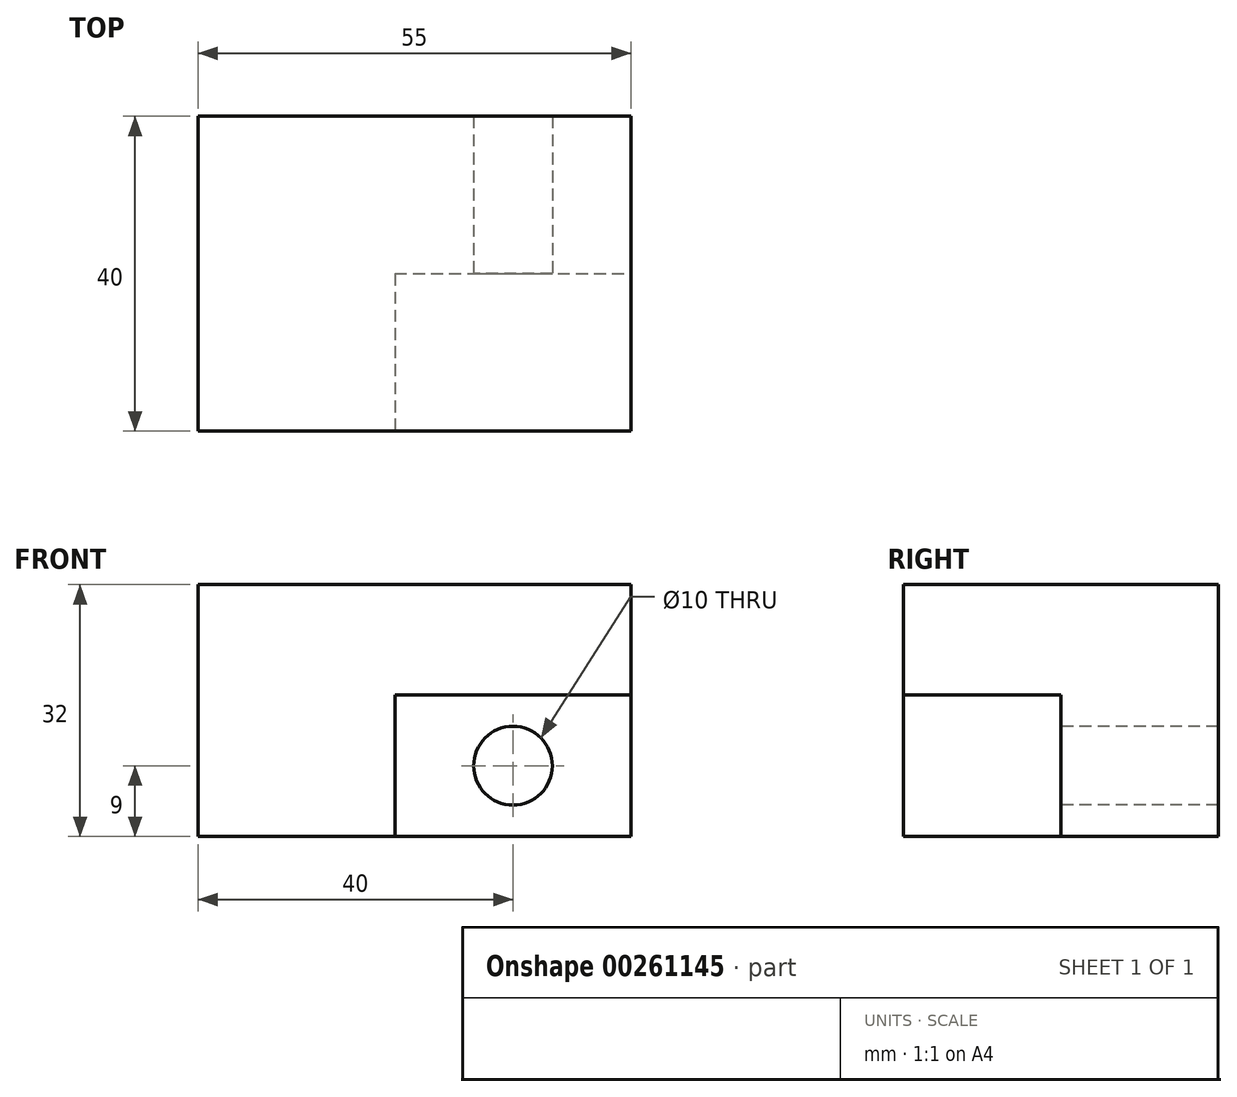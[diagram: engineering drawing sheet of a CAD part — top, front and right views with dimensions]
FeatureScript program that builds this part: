
annotation { "Feature Type Name" : "Feature", "Feature Type Description" : "" }
export const myFeature = defineFeature(function(context is Context, id is Id, definition is map)
    precondition{}
    {
        {
            var Q0;
            Q0=qCreatedBy(makeId("Front.planeOp"),FACE);
            var sketch = newSketch(context, id + "F0", { "sketchPlane" : qUnion([Q0])});
            skLineSegment(sketch, "E0.bottom", {"start": v(0, 0) * mm, "end": v(55, 0) * mm});
            skLineSegment(sketch, "E0.top", {"start": v(0, -32) * mm, "end": v(55, -32) * mm});
            skLineSegment(sketch, "E0.left", {"start": v(0, 0) * mm, "end": v(0, -32) * mm});
            skLineSegment(sketch, "E0.right", {"start": v(55, 0) * mm, "end": v(55, -32) * mm});
            skSolve(sketch);
        }
        {
            var Q0;
            Q0=makeQuery(id+"F0.imprint","IMPRINT",FACE,{"disambiguationData":[TD([[makeQuery(id+"F0.imprint","IMPRINT",EDGE,{"derivedFrom":sQuery(id+"F0.wireOp",EDGE,"E0.bottom")}),-1.0]])]});
            extrude(context, id + "F1", {"entities" : qUnion([Q0]), "depth" : 40 * mm});
        }
        {
            var Q0;
            Q0=makeQuery(id+"F1.opExtrude","CAP_FACE",FACE,{"disambiguationData":[OSD([sQuery(id+"F0.wireOp",EDGE,"E0.bottom"),sQuery(id+"F0.wireOp",EDGE,"E0.top"),sQuery(id+"F0.wireOp",EDGE,"E0.left"),sQuery(id+"F0.wireOp",EDGE,"E0.right")])],"isStart":false});
            var sketch = newSketch(context, id + "F2", { "sketchPlane" : qUnion([Q0])});
            skLineSegment(sketch, "E1.bottom", {"start": v(55, -32) * mm, "end": v(25, -32) * mm});
            skLineSegment(sketch, "E1.top", {"start": v(55, -14) * mm, "end": v(25, -14) * mm});
            skLineSegment(sketch, "E1.left", {"start": v(55, -32) * mm, "end": v(55, -14) * mm});
            skLineSegment(sketch, "E1.right", {"start": v(25, -32) * mm, "end": v(25, -14) * mm});
            skSolve(sketch);
        }
        {
            var Q0;
            Q0=makeQuery(id+"F2.imprint","IMPRINT",FACE,{"disambiguationData":[TD([[makeQuery(id+"F2.imprint","IMPRINT",EDGE,{"derivedFrom":sQuery(id+"F2.wireOp",EDGE,"E1.bottom")}),1.0]])]});
            extrude(context, id + "F3", {"entities" : qUnion([Q0]), "operationType" : NewBodyOperationType.REMOVE, "oppositeDirection" : true, "depth" : 20 * mm});
        }
        {
            var Q0;
            Q0=makeQuery(id+"F3.boolean.opBoolean","COPY",FACE,{"derivedFrom":makeQuery(id+"F3.opExtrude","CAP_FACE",FACE,{"disambiguationData":[OSD([sQuery(id+"F2.wireOp",EDGE,"E1.bottom"),sQuery(id+"F2.wireOp",EDGE,"E1.top"),sQuery(id+"F2.wireOp",EDGE,"E1.left"),sQuery(id+"F2.wireOp",EDGE,"E1.right")])],"isStart":false})});
            var sketch = newSketch(context, id + "F4", { "sketchPlane" : qUnion([Q0])});
            skCircle(sketch, "E2", {"center": v(40, -23) * mm, "radius": 5 * mm});
            skPoint(sketch, "E2.centerSnap0", {"position": v(55, -23) * mm});
            skPoint(sketch, "E2.centerSnap1", {"position": v(40, -32) * mm});
            skSolve(sketch);
        }
        {
            var Q0;
            Q0=makeQuery(id+"F4.imprint","IMPRINT",FACE,{"disambiguationData":[TD([[makeQuery(id+"F4.imprint","IMPRINT",EDGE,{"derivedFrom":sQuery(id+"F4.wireOp",EDGE,"E2")}),1.0]])]});
            extrude(context, id + "F5", {"entities" : qUnion([Q0]), "operationType" : NewBodyOperationType.REMOVE, "endBound" : BoundingType.THROUGH_ALL, "oppositeDirection" : true, "depth" : 25 * mm});
        }
    });
